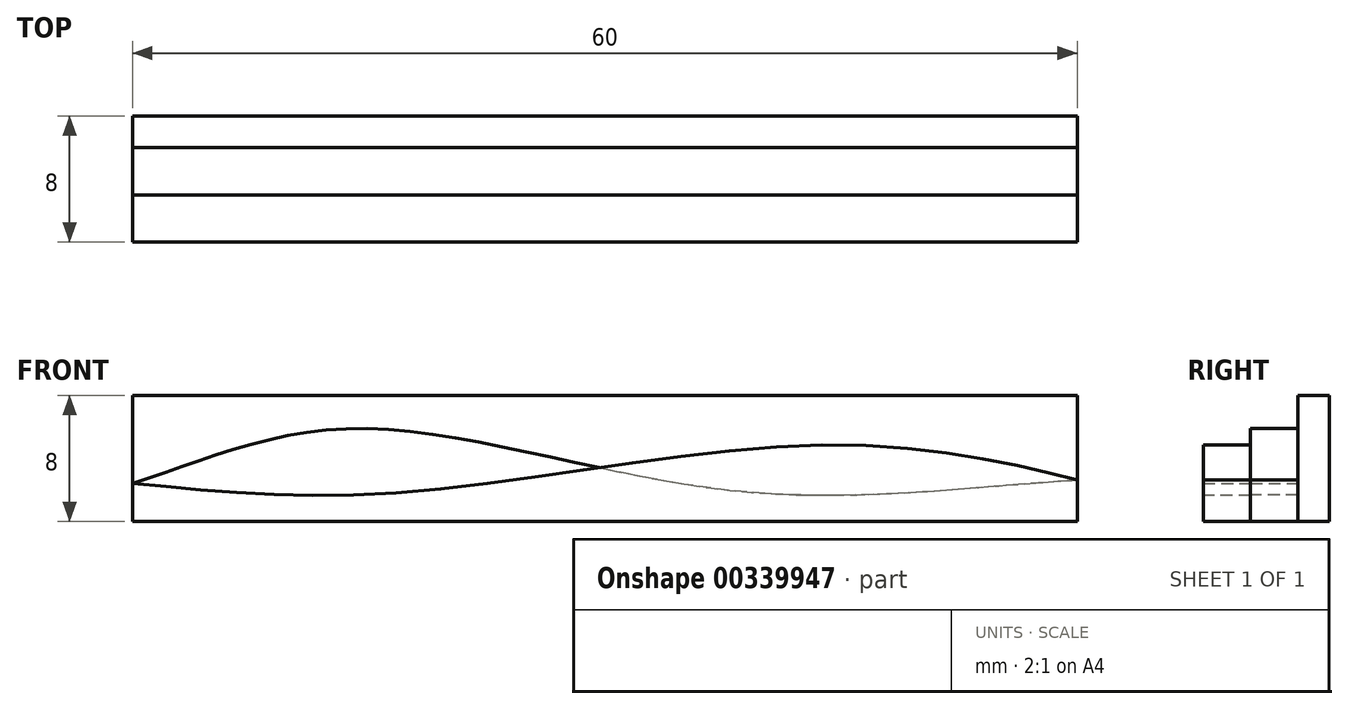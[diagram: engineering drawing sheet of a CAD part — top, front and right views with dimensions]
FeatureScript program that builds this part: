
annotation { "Feature Type Name" : "Feature", "Feature Type Description" : "" }
export const myFeature = defineFeature(function(context is Context, id is Id, definition is map)
    precondition{}
    {
        {
            var Q0;
            Q0=qCreatedBy(makeId("Front.planeOp"),FACE);
            var sketch = newSketch(context, id + "F0", { "sketchPlane" : qUnion([Q0])});
            skLineSegment(sketch, "E0.bottom", {"start": v(-30, 0) * mm, "end": v(30, 0) * mm});
            skLineSegment(sketch, "E0.top", {"start": v(-30, 8) * mm, "end": v(30, 8) * mm});
            skLineSegment(sketch, "E0.left", {"start": v(-30, 0) * mm, "end": v(-30, 8) * mm});
            skLineSegment(sketch, "E0.right", {"start": v(30, 0) * mm, "end": v(30, 8) * mm});
            skSolve(sketch);
        }
        {
            var Q0;
            Q0 = qSketchRegion(id + "F0", true);
            extrude(context, id + "F1", {"entities" : qUnion([Q0]), "depth" : 2 * mm});
        }
        {
            var Q0;
            Q0=makeQuery(id+"F1.opExtrude","CAP_FACE",FACE,{"disambiguationData":[OSD([sQuery(id+"F0.wireOp",EDGE,"E0.bottom"),sQuery(id+"F0.wireOp",EDGE,"E0.top"),sQuery(id+"F0.wireOp",EDGE,"E0.left"),sQuery(id+"F0.wireOp",EDGE,"E0.right")])],"isStart":false});
            var sketch = newSketch(context, id + "F2", { "sketchPlane" : qUnion([Q0])});
            skLineSegment(sketch, "E1.0.0", {"start": v(30, 8) * mm, "end": v(-30, 8) * mm});
            skLineSegment(sketch, "E1.0.1", {"start": v(-30, 8) * mm, "end": v(-30, 0) * mm});
            skLineSegment(sketch, "E1.0.2", {"start": v(-30, 0) * mm, "end": v(30, 0) * mm});
            skLineSegment(sketch, "E1.0.3", {"start": v(30, 0) * mm, "end": v(30, 8) * mm});
            skFitSpline(sketch, "E2", {"points": [v(-30, 2.43) * mm, v(-16.07, 5.9) * mm, v(7.64, 2.01) * mm, v(30, 2.64) * mm], "startDerivative": vector(44.9, 14) * mm, "endDerivative": vector(60.1, 3.6) * mm});
            skSolve(sketch);
        }
        {
            var Q0;
            {var subQ0=sQuery(id+"F2.wireOp",EDGE,"E1.0.2");Q0=makeQuery(id+"F2.imprint","IMPRINT",FACE,{"disambiguationData":[TD([[makeQuery(id+"F2.imprint","IMPRINT",EDGE,{"derivedFrom":subQ0}),1.0]])]});}
            extrude(context, id + "F3", {"entities" : qUnion([Q0]), "depth" : 3 * mm});
        }
        {
            var Q0;
            Q0=makeQuery(id+"F3.opExtrude","CAP_FACE",FACE,{"disambiguationData":[OSD([sQuery(id+"F2.wireOp",EDGE,"E1.0.1"),sQuery(id+"F2.wireOp",EDGE,"E1.0.2"),sQuery(id+"F2.wireOp",EDGE,"E1.0.3"),sQuery(id+"F2.wireOp",EDGE,"E2")])],"isStart":false});
            var sketch = newSketch(context, id + "F4", { "sketchPlane" : qUnion([Q0])});
            skLineSegment(sketch, "E3.0.0", {"start": v(30, 8) * mm, "end": v(-30, 8) * mm});
            skLineSegment(sketch, "E3.0.1", {"start": v(-30, 8) * mm, "end": v(-30, 0) * mm});
            skLineSegment(sketch, "E3.0.2", {"start": v(-30, 0) * mm, "end": v(30, 0) * mm});
            skLineSegment(sketch, "E3.0.3", {"start": v(30, 0) * mm, "end": v(30, 8) * mm});
            skFitSpline(sketch, "E4", {"points": [v(-30, 2.43) * mm, v(-12.98, 1.83) * mm, v(14.03, 4.86) * mm, v(30, 2.64) * mm], "startDerivative": vector(48.32, -4.78) * mm, "endDerivative": vector(39.65, -10.2) * mm});
            skSolve(sketch);
        }
        {
            var Q0;
            {var subQ6=sQuery(id+"F4.wireOp",EDGE,"E3.0.2");Q0=makeQuery(id+"F4.imprint","IMPRINT",FACE,{"disambiguationData":[TD([[makeQuery(id+"F4.imprint","IMPRINT",EDGE,{"derivedFrom":subQ6}),1.0]])]});}
            var Q1;
            {var subQ0=sQuery(id+"F4.wireOp",EDGE,"E4");var subQ1=makeQuery(id+"F3.opExtrude","CAP_EDGE",EDGE,{"disambiguationData":[OSD([sQuery(id+"F2.wireOp",EDGE,"E2")])],"isStart":false});var subQ3=makeQuery(id+"F4.imprint","INTERSECT",VERTEX,{"derivedFrom":[subQ1,subQ0]});Q1=makeQuery(id+"F4.imprint","IMPRINT",FACE,{"disambiguationData":[TD([[makeQuery(id+"F4.imprint","IMPRINT",EDGE,{"disambiguationData":[TD([[subQ3,-1.0]])],"derivedFrom":subQ0}),-1.0]])]});}
            extrude(context, id + "F5", {"entities" : qUnion([Q0, Q1]), "depth" : 3 * mm});
        }
    });
